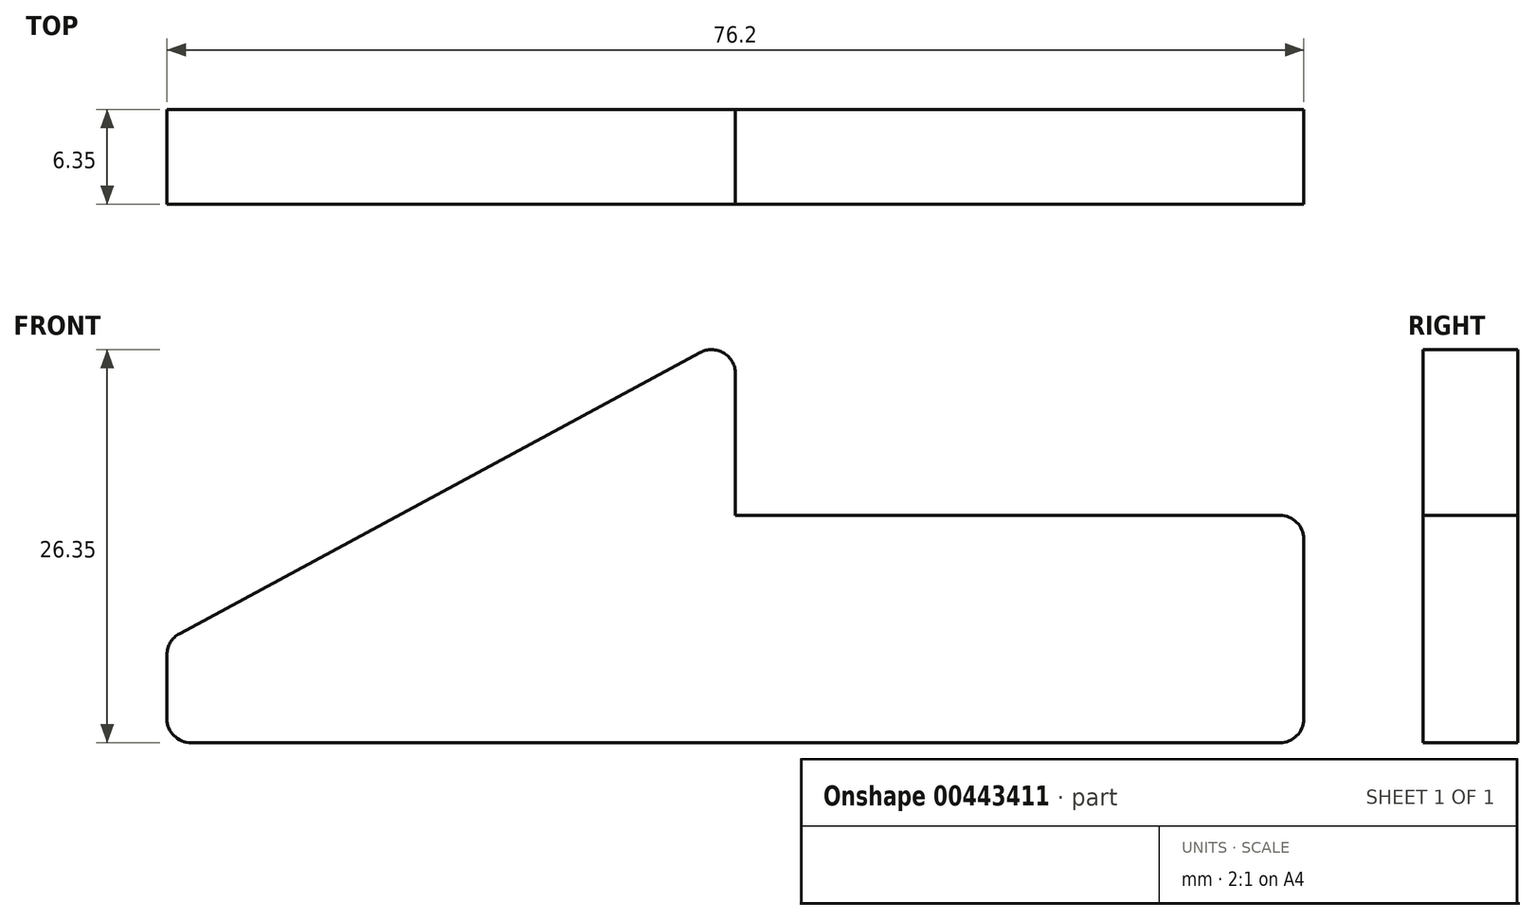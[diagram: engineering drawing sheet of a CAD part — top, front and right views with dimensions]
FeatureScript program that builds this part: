
annotation { "Feature Type Name" : "Feature", "Feature Type Description" : "" }
export const myFeature = defineFeature(function(context is Context, id is Id, definition is map)
    precondition{}
    {
        {
            var Q0;
            Q0=qCreatedBy(makeId("Front.planeOp"),FACE);
            var sketch = newSketch(context, id + "F0", { "sketchPlane" : qUnion([Q0])});
            skLineSegment(sketch, "E0", {"start": v(-36.5, 0) * mm, "end": v(36.5, 0) * mm});
            skLineSegment(sketch, "E1", {"start": v(38.1, 1.6) * mm, "end": v(38.1, 13.64) * mm});
            skLineSegment(sketch, "E2", {"start": v(36.5, 15.24) * mm, "end": v(0, 15.24) * mm});
            skLineSegment(sketch, "E3", {"start": v(0, 15.24) * mm, "end": v(0, 24.75) * mm});
            skLineSegment(sketch, "E4", {"start": v(-38.1, 5.9) * mm, "end": v(-38.1, 1.6) * mm});
            skPoint(sketch, "E5.visualSharp", {"position": v(0, 27.43) * mm});
            skLineSegment(sketch, "E5.filletArc", {"start": v(0, 27.43) * mm, "end": v(0, 27.43) * mm});
            skLineSegment(sketch, "E6", {"start": v(-37.26, 7.31) * mm, "end": v(-2.36, 26.16) * mm});
            skArc(sketch, "E7.filletArc", {"start": v(0, 24.75) * mm, "mid": v(-0.78, 26.12) * mm, "end": v(-2.36, 26.16) * mm});
            skPoint(sketch, "E8.visualSharp", {"position": v(-38.1, 6.86) * mm});
            skArc(sketch, "E8.filletArc", {"start": v(-37.26, 7.31) * mm, "mid": v(-37.87, 6.72) * mm, "end": v(-38.1, 5.9) * mm});
            skPoint(sketch, "E9.visualSharp", {"position": v(-38.1, 0) * mm});
            skArc(sketch, "E9.filletArc", {"start": v(-38.1, 1.6) * mm, "mid": v(-37.63, 0.47) * mm, "end": v(-36.5, 0) * mm});
            skPoint(sketch, "E10.visualSharp", {"position": v(38.1, 0) * mm});
            skArc(sketch, "E10.filletArc", {"start": v(36.5, 0) * mm, "mid": v(37.63, 0.47) * mm, "end": v(38.1, 1.6) * mm});
            skPoint(sketch, "E11.visualSharp", {"position": v(38.1, 15.24) * mm});
            skArc(sketch, "E11.filletArc", {"start": v(38.1, 13.64) * mm, "mid": v(37.63, 14.77) * mm, "end": v(36.5, 15.24) * mm});
            skSolve(sketch);
        }
        {
            var Q0;
            Q0 = qSketchRegion(id + "F0", true);
            extrude(context, id + "F1", {"entities" : qUnion([Q0]), "depth" : 6.35 * mm});
        }
    });
